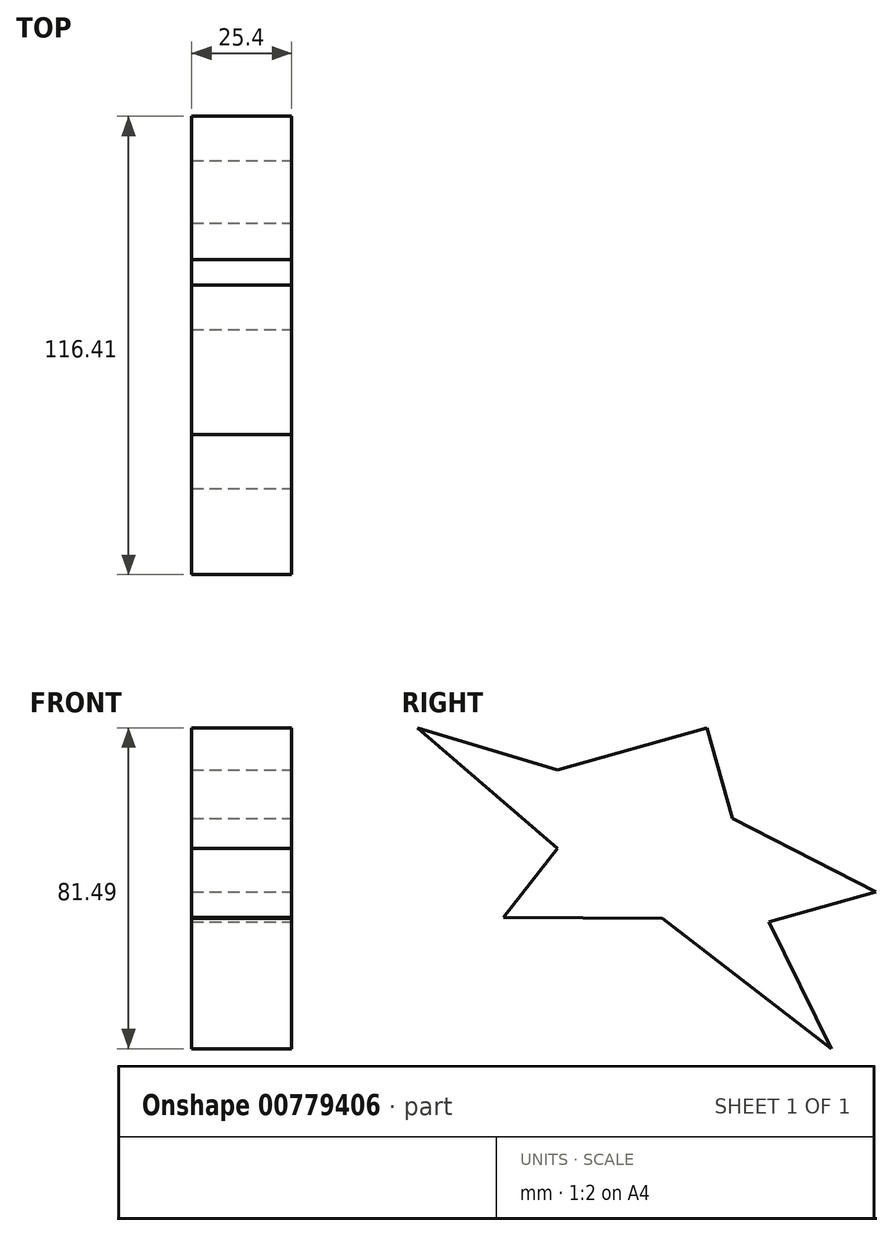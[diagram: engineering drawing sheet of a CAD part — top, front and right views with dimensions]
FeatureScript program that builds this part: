
annotation { "Feature Type Name" : "Feature", "Feature Type Description" : "" }
export const myFeature = defineFeature(function(context is Context, id is Id, definition is map)
    precondition{}
    {
        {
            var Q0;
            Q0=qCreatedBy(makeId("Right.planeOp"),FACE);
            var sketch = newSketch(context, id + "F0", { "sketchPlane" : qUnion([Q0])});
            skLineSegment(sketch, "E0", {"start": v(-13.62, -37.47) * mm, "end": v(0, -19.95) * mm});
            skLineSegment(sketch, "E1", {"start": v(-35.5, 10.68) * mm, "end": v(0, 0) * mm});
            skLineSegment(sketch, "E2", {"start": v(-35.5, 10.68) * mm, "end": v(0, -19.95) * mm});
            skLineSegment(sketch, "E3", {"start": v(38.06, 10.68) * mm, "end": v(0, 0) * mm});
            skLineSegment(sketch, "E4", {"start": v(38.06, 10.68) * mm, "end": v(44.51, -12.3) * mm});
            skLineSegment(sketch, "E5", {"start": v(44.51, -12.3) * mm, "end": v(80.91, -31.03) * mm});
            skLineSegment(sketch, "E6", {"start": v(80.91, -31.03) * mm, "end": v(53.8, -38.64) * mm});
            skLineSegment(sketch, "E7", {"start": v(53.8, -38.64) * mm, "end": v(69.64, -70.8) * mm});
            skLineSegment(sketch, "E8", {"start": v(26.74, -37.7) * mm, "end": v(-13.62, -37.47) * mm});
            skLineSegment(sketch, "E9", {"start": v(26.74, -37.7) * mm, "end": v(69.64, -70.8) * mm});
            skSolve(sketch);
        }
        {
            var Q0;
            Q0=makeQuery(id+"F0.imprint","IMPRINT",FACE,{"disambiguationData":[TD([[makeQuery(id+"F0.imprint","IMPRINT",EDGE,{"derivedFrom":sQuery(id+"F0.wireOp",EDGE,"E0")}),-1.0]])]});
            extrude(context, id + "F1", {"entities" : qUnion([Q0]), "oppositeDirection" : true, "depth" : 25.4 * mm, "offsetDistance" : 25.4 * mm});
        }
    });
